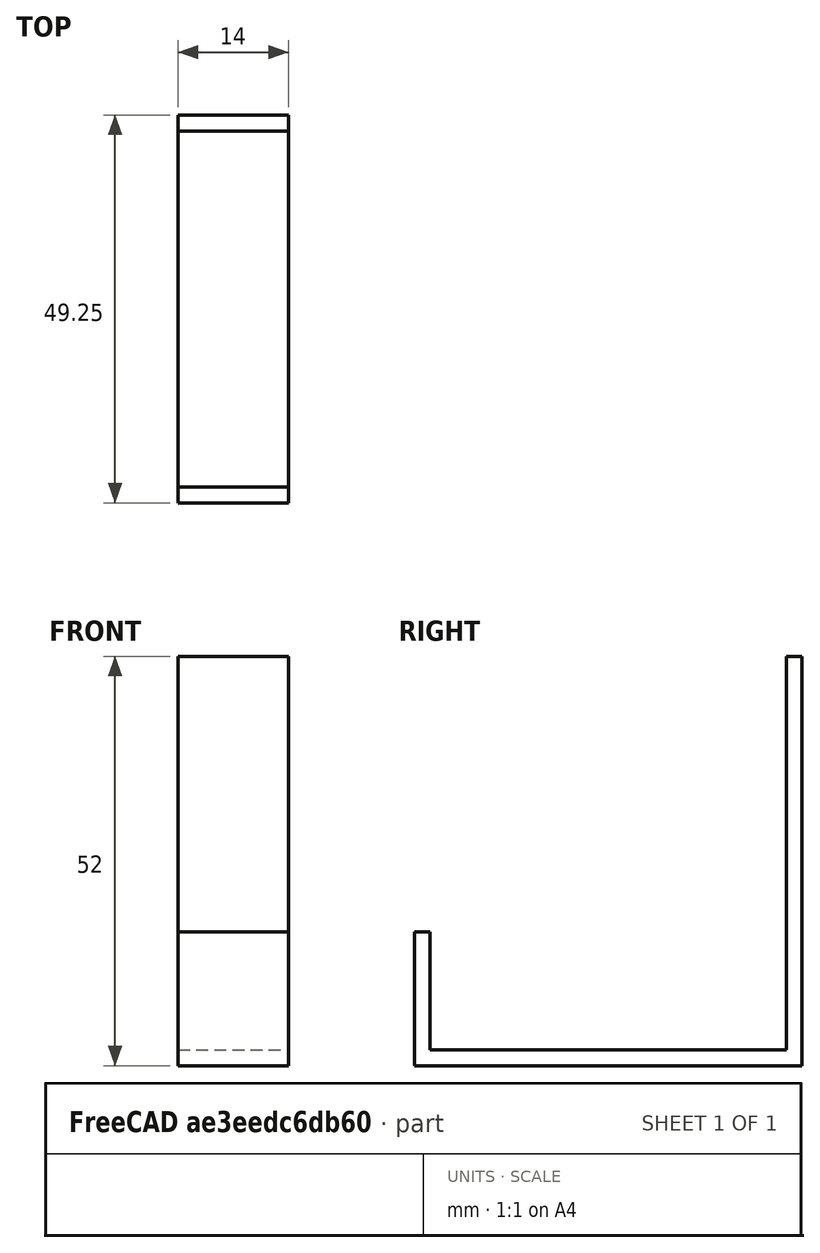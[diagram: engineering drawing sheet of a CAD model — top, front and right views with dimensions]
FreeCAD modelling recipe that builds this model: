
FCSTD DOCUMENT  (FreeCAD 0.20R29177 +426 (Git))
Label: Nomad Kit
License: All rights reserved
LicenseURL: http://en.wikipedia.org/wiki/All_rights_reserved
objects: Sketcher::SketchObject×1, PartDesign::Pad×1, PartDesign::Body×1, App::Part×1
note: 4 computed .brp shape members not serialized (recipe doc carries the construction recipe); baked Part::Feature solids carry a one-line shape summary decoded from their .brp

FEATURE [Sketcher::SketchObject] Sketch
  FullyConstrained = true
  MapMode = 5
  Placement = pos=(0,0,0) rot=(0.57735,0.57735,0.57735;2.0944rad)
  Support = -> [YZ_Plane001]
  sketch-geometry (9):
    g0: LineSegment StartX=0 StartY=0 StartZ=0 EndX=0 EndY=17 EndZ=0
    g1: LineSegment StartX=0 StartY=17 StartZ=0 EndX=2 EndY=17 EndZ=0
    g2: LineSegment StartX=2 StartY=17 StartZ=0 EndX=2 EndY=2 EndZ=0
    g3: LineSegment StartX=2 StartY=2 StartZ=0 EndX=47.25 EndY=2 EndZ=0
    g4: LineSegment StartX=47.25 StartY=2 StartZ=0 EndX=47.25 EndY=52 EndZ=0
    g5: LineSegment StartX=47.25 StartY=52 StartZ=0 EndX=49.25 EndY=52 EndZ=0
    g6: LineSegment StartX=49.25 StartY=52 StartZ=0 EndX=49.25 EndY=0 EndZ=0
    g7: LineSegment StartX=49.25 StartY=0 StartZ=0 EndX=0 EndY=0 EndZ=0
    g8: LineSegment StartX=2 StartY=2 StartZ=0 EndX=2 EndY=0 EndZ=0
  constraints (26):
    c: Coincident(g0,g-1)
    c: Vertical(g0)
    c: Coincident(g1,g0)
    c: Horizontal(g1)
    c: Coincident(g2,g1)
    c: Coincident(g3,g2)
    c: Horizontal(g3)
    c: Coincident(g4,g3)
    c: Vertical(g4)
    c: Coincident(g5,g4)
    c: Horizontal(g5)
    c: Coincident(g6,g5)
    c: PointOnObject(g6,g-1)
    c: Vertical(g6)
    c: Coincident(g7,g6)
    c: Coincident(g7,g0)
    c: Vertical(g2)
    c: Coincident(g8,g2)
    c: PointOnObject(g8,g7)
    c: Vertical(g8)
    c: Equal(g1,g8)
    c: Equal(g8,g5)
    c: Distance(g3) = 45.25
    c: Distance(g1) = 2
    c: Distance(g2) = 15
    c: Distance(g4) = 50
FEATURE [PartDesign::Pad] Pad
  Direction = (1,-2e-16,3e-16)
  Length = 14
  Length2 = 10
  Placement = pos=(0,0,0) rot=(0.57735,0.57735,0.57735;2.0944rad)
  Profile = -> Sketch
  ReferenceAxis = -> Sketch [N_Axis]
  Type = 0
FEATURE [PartDesign::Body] Body
  Group = -> [Sketch,Pad]
  Origin = -> Origin001
  Tip = -> Pad
FEATURE [App::Part] Part
  Group = -> [Body]
  Origin = -> Origin
